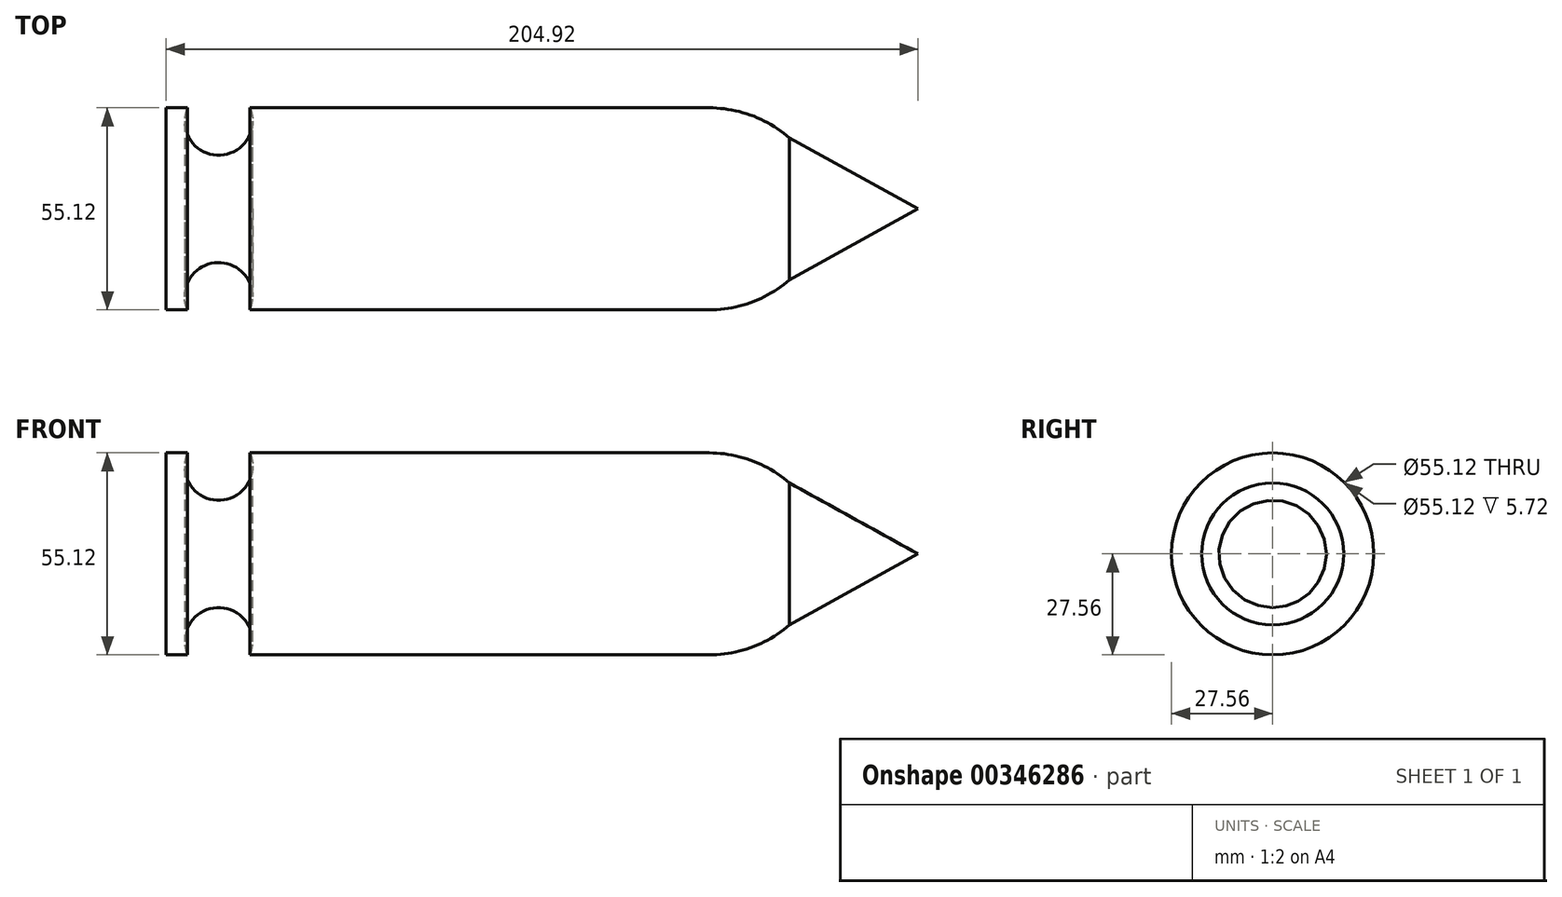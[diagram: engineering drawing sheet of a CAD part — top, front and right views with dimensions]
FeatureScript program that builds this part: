
annotation { "Feature Type Name" : "Feature", "Feature Type Description" : "" }
export const myFeature = defineFeature(function(context is Context, id is Id, definition is map)
    precondition{}
    {
        {
            var Q0;
            Q0=qCreatedBy(makeId("Front.planeOp"),FACE);
            var sketch = newSketch(context, id + "F0", { "sketchPlane" : qUnion([Q0])});
            skPoint(sketch, "E0", {"position": v(0, 27.56) * mm});
            skLineSegment(sketch, "E1", {"start": v(0, 0) * mm, "end": v(0, 27.56) * mm});
            skLineSegment(sketch, "E2", {"start": v(0, 27.56) * mm, "end": v(5.72, 27.56) * mm});
            skPoint(sketch, "E3", {"position": v(22.84, 27.56) * mm});
            skPoint(sketch, "E4", {"position": v(5.72, 27.56) * mm});
            skArc(sketch, "E5", {"start": v(5.72, 27.56) * mm, "mid": v(14.28, 14.64) * mm, "end": v(22.84, 27.56) * mm});
            skLineSegment(sketch, "E6", {"start": v(22.84, 27.56) * mm, "end": v(28.56, 27.56) * mm});
            skLineSegment(sketch, "E7", {"start": v(22.49, 27.56) * mm, "end": v(22.84, 27.56) * mm});
            skLineSegment(sketch, "E8", {"start": v(28.56, 27.56) * mm, "end": v(147.97, 27.56) * mm});
            skPoint(sketch, "E9", {"position": v(169.92, 19.36) * mm});
            skArc(sketch, "E10", {"start": v(147.97, 27.56) * mm, "mid": v(159.69, 25.44) * mm, "end": v(169.92, 19.36) * mm});
            skLineSegment(sketch, "E11", {"start": v(169.92, 19.36) * mm, "end": v(204.92, 0) * mm});
            skSolve(sketch);
        }
        {
            var Q0;
            Q0=qCreatedBy(makeId("Front.planeOp"),FACE);
            var sketch = newSketch(context, id + "F1", { "sketchPlane" : qUnion([Q0])});
            skLineSegment(sketch, "E12", {"start": v(208.65, 0) * mm, "end": v(223.7, 0) * mm});
            skSolve(sketch);
        }
        {
            var Q0;
            Q0 = qSketchRegion(id + "F0", true);
            var Q1;
            Q1=sQuery(id+"F0.wireOp",EDGE,"E1");
            var Q2;
            Q2=sQuery(id+"F0.wireOp",EDGE,"E2");
            var Q3;
            Q3=sQuery(id+"F0.wireOp",EDGE,"E5");
            var Q4;
            Q4=sQuery(id+"F0.wireOp",EDGE,"E6");
            var Q5;
            Q5=sQuery(id+"F0.wireOp",EDGE,"E8");
            var Q6;
            Q6=sQuery(id+"F0.wireOp",EDGE,"E10");
            var Q7;
            Q7=sQuery(id+"F0.wireOp",EDGE,"E11");
            var Q8;
            Q8=sQuery(id+"F1.wireOp",EDGE,"E12");
            revolve(context, id + "F2", {"bodyType" : ToolBodyType.SURFACE, "entities" : qUnion([Q0]), "surfaceEntities" : qUnion([Q1, Q2, Q3, Q4, Q5, Q6, Q7]), "axis" : qUnion([Q8]), "revolveType" : RevolveType.FULL});
        }
    });
